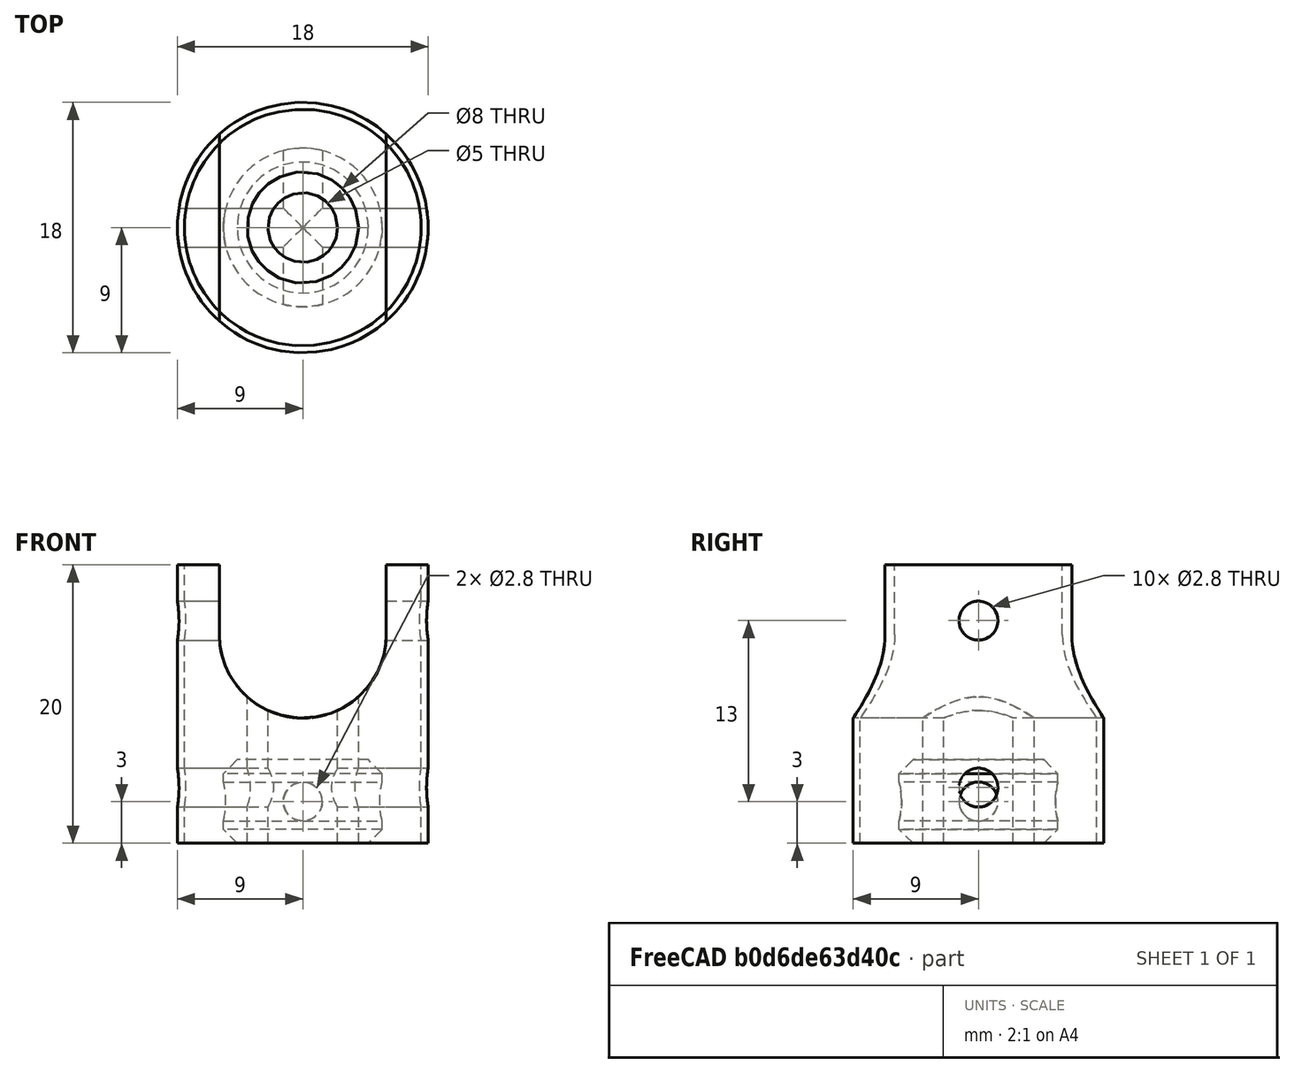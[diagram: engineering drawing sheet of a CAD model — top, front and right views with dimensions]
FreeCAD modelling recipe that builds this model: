
FCSTD DOCUMENT  (FreeCAD 0.14R3700 (Git))
Label: unijoint
License: CC-BY 3.0
LicenseURL: http://creativecommons.org/licenses/by/3.0/
objects: Part::Cylinder×13, Part::Cut×5, Part::MultiFuse×3, Part::Box×2, Part::Chamfer×1
note: 24 computed .brp shape members not serialized (recipe doc carries the construction recipe); baked Part::Feature solids carry a one-line shape summary decoded from their .brp

FEATURE [Part::Cylinder] Cylinder001  label="cyl cutout joiner 5"
  Angle = 360
  Height = 20
  Placement = pos=(0,10,15) rot=(1,0,0;1.5708rad)
  Radius = 6
FEATURE [Part::Box] Box  label="cube cutout for joiner 5"
  Height = 10
  Length = 12
  Placement = pos=(-6,-10,15) rot=(0,0,1;0rad)
  Width = 20
FEATURE [Part::Cylinder] Cylinder002  label="Base 8"
  Angle = 360
  Height = 20
  Radius = 8.5
FEATURE [Part::Cylinder] Cylinder003  label="joiner pin holes 5"
  Angle = 360
  Height = 22
  Placement = pos=(-11,0,16) rot=(0,1,0;1.5708rad)
  Radius = 1.4
FEATURE [Part::Cylinder] Cylinder004  label="joiner base"
  Angle = 360
  Height = 6
  Radius = 5.7
FEATURE [Part::Cylinder] Cylinder005  label="joiner pin 1"
  Angle = 360
  Height = 18
  Placement = pos=(0,9,3) rot=(1,0,0;1.5708rad)
  Radius = 1.4
FEATURE [Part::Cylinder] Cylinder007  label="5mm"
  Angle = 360
  Height = 12
  Placement = pos=(0,0,-0.5) rot=(0,0,1;0rad)
  Radius = 2.5
FEATURE [Part::Cylinder] Cylinder008  label="locking pin 5"
  Angle = 360
  Height = 20
  Placement = pos=(-10,0,4) rot=(0,1,0;1.5708rad)
  Radius = 1.4
FEATURE [Part::Cylinder] Cylinder  label="Base 5"
  Angle = 360
  Height = 20
  Radius = 9
FEATURE [Part::Cylinder] Cylinder012  label="joiner pin 2"
  Angle = 360
  Height = 18
  Placement = pos=(-9,0,3) rot=(0,1,0;1.5708rad)
  Radius = 1.4
FEATURE [Part::MultiFuse] Fusion002  label="joiner pins"
  Shapes = -> [Cylinder012,Cylinder005]
FEATURE [Part::Cut] Cut009
  Base = -> Cylinder004
  Tool = -> Fusion002
FEATURE [Part::Chamfer] Chamfer  label="joiner"
  Base = -> Cut009
  Edges = 2 edges r=1: [Edge4,Edge6]
FEATURE [Part::MultiFuse] Fusion  label="cutouts"
  Shapes = -> [Cylinder003,Cylinder008,Cylinder001,Box]
FEATURE [Part::Box] Box001  label="cube cutout for joiner 006"
  Height = 10
  Length = 12
  Placement = pos=(-6,-10,15) rot=(0,0,1;0rad)
  Width = 20
FEATURE [Part::Cylinder] Cylinder013  label="cyl cutout joiner 006"
  Angle = 360
  Height = 20
  Placement = pos=(0,10,15) rot=(1,0,0;1.5708rad)
  Radius = 6
FEATURE [Part::Cylinder] Cylinder014  label="locking pin 006"
  Angle = 360
  Height = 20
  Placement = pos=(-10,0,4) rot=(0,1,0;1.5708rad)
  Radius = 1.4
FEATURE [Part::Cylinder] Cylinder015  label="joiner pin holes 006"
  Angle = 360
  Height = 22
  Placement = pos=(-11,0,16) rot=(0,1,0;1.5708rad)
  Radius = 1.4
FEATURE [Part::MultiFuse] Fusion003  label="cutouts001"
  Shapes = -> [Cylinder015,Cylinder014,Cylinder013,Box001]
FEATURE [Part::Cut] Cut
  Base = -> Cylinder002
  Tool = -> Fusion
FEATURE [Part::Cut] Cut010
  Base = -> Cylinder
  Tool = -> Fusion003
FEATURE [Part::Cylinder] Cylinder016  label="5mm001"
  Angle = 360
  Height = 12
  Placement = pos=(0,0,-0.5) rot=(0,0,1;0rad)
  Radius = 4
FEATURE [Part::Cut] Cut011
  Base = -> Cut
  Tool = -> Cylinder007
FEATURE [Part::Cut] Cut012
  Base = -> Cut010
  Tool = -> Cylinder016
